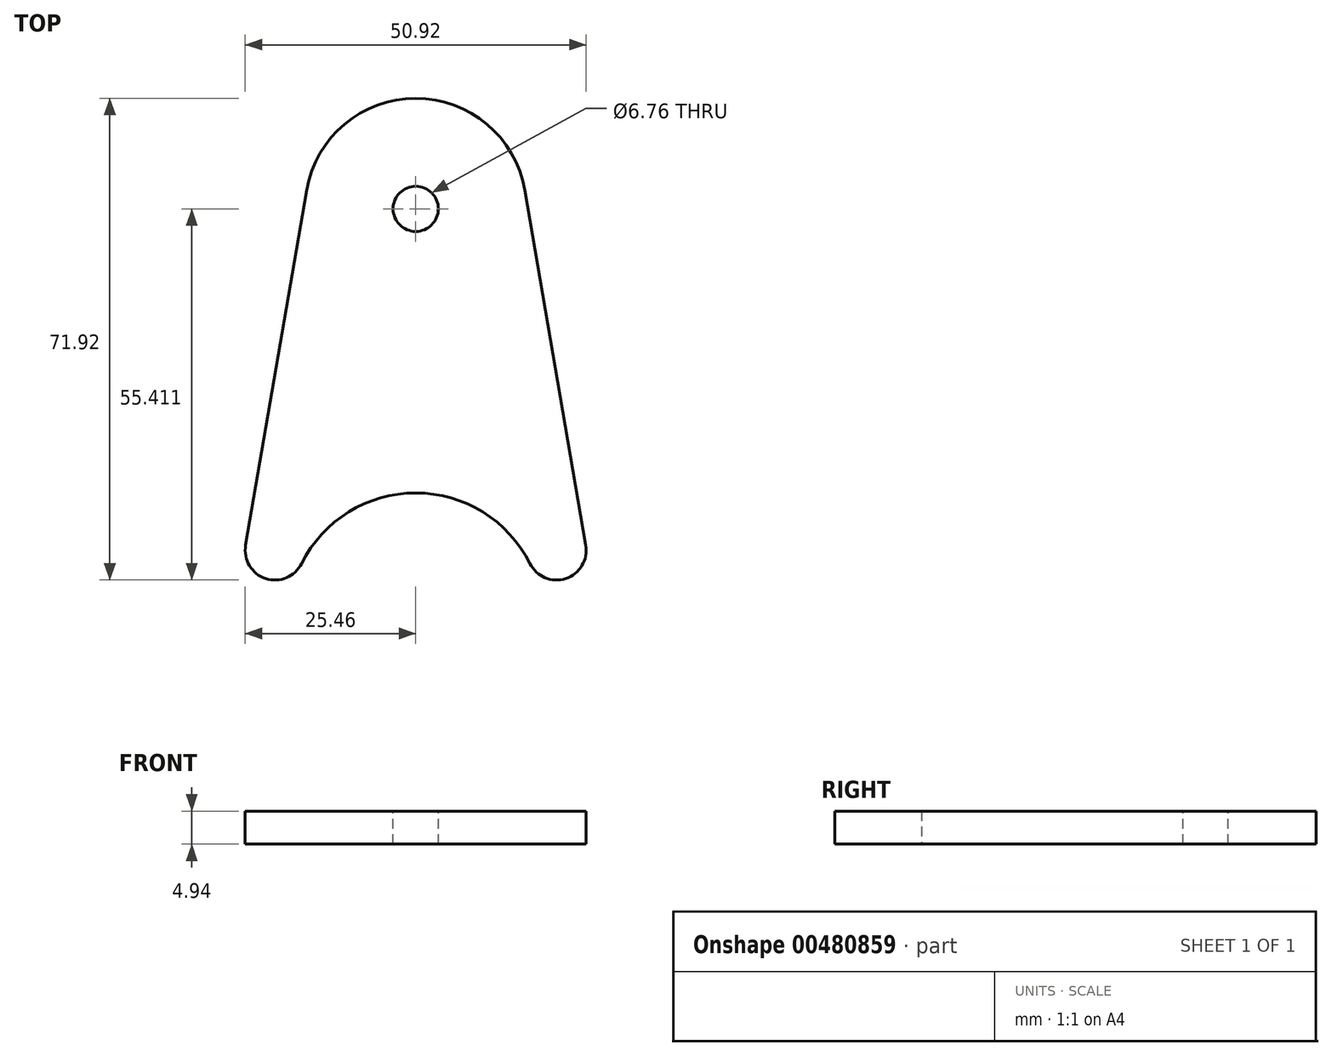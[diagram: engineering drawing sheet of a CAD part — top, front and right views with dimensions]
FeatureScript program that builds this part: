
annotation { "Feature Type Name" : "Feature", "Feature Type Description" : "" }
export const myFeature = defineFeature(function(context is Context, id is Id, definition is map)
    precondition{}
    {
        {
            var Q0;
            Q0=qCreatedBy(makeId("Top.planeOp"),FACE);
            var sketch = newSketch(context, id + "F0", { "sketchPlane" : qUnion([Q0])});
            skLineSegment(sketch, "E0", {"start": v(0, -49.37) * mm, "end": v(0, 65.55) * mm, "construction": true});
            skArc(sketch, "E1", {"start": v(0, 37.67) * mm, "mid": v(-10.64, 33.79) * mm, "end": v(-16.27, 23.96) * mm});
            skArc(sketch, "E2", {"start": v(0, -21.26) * mm, "mid": v(-10.02, -24.1) * mm, "end": v(-17.04, -31.8) * mm});
            skLineSegment(sketch, "E3", {"start": v(-25.4, -29.06) * mm, "end": v(-16.27, 23.96) * mm});
            skArc(sketch, "E4.MirrorCS", {"start": v(0, 37.67) * mm, "mid": v(10.64, 33.79) * mm, "end": v(16.27, 23.96) * mm});
            skLineSegment(sketch, "E5.MirrorCS", {"start": v(25.4, -29.06) * mm, "end": v(16.27, 23.96) * mm});
            skArc(sketch, "E6.MirrorCS", {"start": v(0, -21.26) * mm, "mid": v(10.02, -24.1) * mm, "end": v(17.04, -31.8) * mm});
            skArc(sketch, "E7", {"start": v(-25.4, -29.06) * mm, "mid": v(-22.4, -34.03) * mm, "end": v(-17.04, -31.8) * mm});
            skArc(sketch, "E8.MirrorCS", {"start": v(25.4, -29.06) * mm, "mid": v(22.4, -34.03) * mm, "end": v(17.04, -31.8) * mm});
            skSolve(sketch);
        }
        {
            var Q0;
            Q0=qSketchRegion(id+"F0",true);
            extrude(context, id + "F1", {"entities" : qUnion([Q0]), "depth" : 4.94 * mm});
        }
        {
            var Q0;
            Q0=makeQuery(id+"F1.opExtrude","CAP_FACE",FACE,{"disambiguationData":[OSD([sQuery(id+"F0.wireOp",EDGE,"E1"),sQuery(id+"F0.wireOp",EDGE,"E2"),sQuery(id+"F0.wireOp",EDGE,"E3"),sQuery(id+"F0.wireOp",EDGE,"E4.MirrorCS"),sQuery(id+"F0.wireOp",EDGE,"E5.MirrorCS"),sQuery(id+"F0.wireOp",EDGE,"E6.MirrorCS"),sQuery(id+"F0.wireOp",EDGE,"E7"),sQuery(id+"F0.wireOp",EDGE,"E8.MirrorCS")])],"isStart":false});
            var sketch = newSketch(context, id + "F2", { "sketchPlane" : qUnion([Q0])});
            skPoint(sketch, "E9", {"position": v(0, 21.16) * mm});
            skSolve(sketch);
        }
        {
            var Q0;
            Q0=sQuery(id+"F2.wireOp",VERTEX,"E9");
            var Q1;
            Q1=makeQuery(id+"F1.opExtrude","SWEPT_BODY",BODY,{"disambiguationData":[OSD([sQuery(id+"F0.wireOp",EDGE,"E1"),sQuery(id+"F0.wireOp",EDGE,"E2"),sQuery(id+"F0.wireOp",EDGE,"E3"),sQuery(id+"F0.wireOp",EDGE,"E4.MirrorCS"),sQuery(id+"F0.wireOp",EDGE,"E5.MirrorCS"),sQuery(id+"F0.wireOp",EDGE,"E6.MirrorCS"),sQuery(id+"F0.wireOp",EDGE,"E7"),sQuery(id+"F0.wireOp",EDGE,"E8.MirrorCS")])]});
            hole(context, id + "F3", {"style" : HoleStyle.SIMPLE, "endStyle" : HoleEndStyle.THROUGH, "standardTappedOrClearance" : lookupTablePath({ "standard" : "ANSI", "fit" : "Normal (ASME)", "size" : "1/4", "type" : "Clearance" }), "standardBlindInLast" : lookupTablePath({ "fit" : "Free", "standard" : "ANSI", "size" : "1/4", "type" : "Clearance" }), "holeDiameter" : 6.76 * mm, "isTappedThrough" : true, "tappedDepth" : 12.7 * mm, "tapClearance" : 3, "locations" : qUnion([Q0]), "scope" : qUnion([Q1])});
        }
    });
